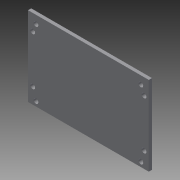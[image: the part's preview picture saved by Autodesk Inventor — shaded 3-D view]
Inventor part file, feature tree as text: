
AUTODESK INVENTOR PART (.ipt)
format: ipt  version: 2013 (Build 170138000, 138)  size: 115,712 bytes
history: native  units: mm
features: extrude x3, sketch x3, other x1
ambient origin geometry x8: Origin, YZ Plane, XZ Plane, XY Plane, X Axis, Y Axis, Z Axis, Center Point
feature tree (7):
  other  "ソリッド1"
  extrude  "押し出し1"  Depth=76.0mm
  extrude  "押し出し2"  Depth=50.0mm
  extrude  "押し出し3"  Depth=35.0mm
  sketch  "スケッチ1"
  sketch  "スケッチ2"
  sketch  "スケッチ3"
